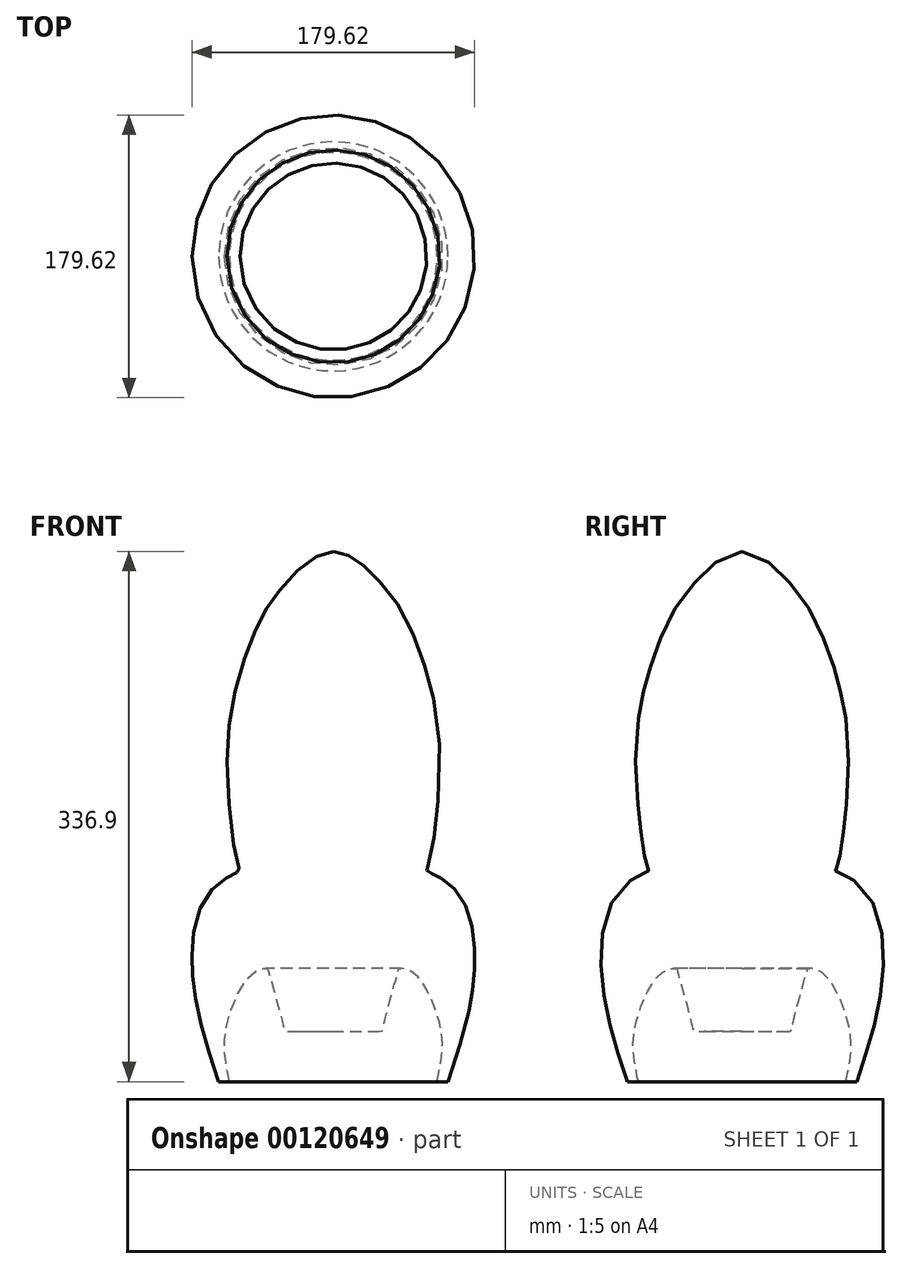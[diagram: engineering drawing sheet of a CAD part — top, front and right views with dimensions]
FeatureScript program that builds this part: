
annotation { "Feature Type Name" : "Feature", "Feature Type Description" : "" }
export const myFeature = defineFeature(function(context is Context, id is Id, definition is map)
    precondition{}
    {
        {
            var Q0;
            Q0=qCreatedBy(makeId("Front.planeOp"),FACE);
            var sketch = newSketch(context, id + "F0", { "sketchPlane" : qUnion([Q0])});
            skLineSegment(sketch, "E0", {"start": v(0, 114.68) * mm, "end": v(0, -121.07) * mm, "construction": true});
            skPoint(sketch, "E1", {"position": v(0, 172.24) * mm});
            skFitSpline(sketch, "E2", {"points": [v(-72.77, -166.31) * mm, v(-84.52, -128.06) * mm, v(-89.05, -101.48) * mm, v(-89.66, -81.76) * mm, v(-84.76, -56.41) * mm, v(-72.5, -39.7) * mm, v(-63.44, -34.55) * mm, v(-60.38, -33.08) * mm, v(-59.4, -32.71) * mm, v(-60.25, -30.02) * mm, v(-67.36, 26.2) * mm, v(-61.85, 84.61) * mm, v(-47.02, 126) * mm, v(-35.24, 144.53) * mm, v(-13.84, 165.57) * mm, v(0, 170.6) * mm], "startDerivative": vector(-145.39, 429.1) * mm, "endDerivative": vector(234.13, 44.8) * mm});
            skLineSegment(sketch, "E3", {"start": v(-72.77, -166.31) * mm, "end": v(-65.98, -166.31) * mm});
            skFitSpline(sketch, "E4", {"points": [v(-65.98, -166.31) * mm, v(-68.4, -152.9) * mm, v(-68.22, -132.99) * mm, v(-52.46, -98.52) * mm, v(-43.36, -94.29) * mm, v(-42.42, -94.32) * mm, v(-41.67, -94.42) * mm, v(-41.45, -95.04) * mm, v(-39.3, -102.66) * mm, v(-33.95, -122.35) * mm, v(-31.41, -132.76) * mm, v(-31.12, -133.88) * mm, v(-30.78, -134.17) * mm, v(-29.95, -134.31) * mm, v(0, -134.22) * mm], "startDerivative": vector(-30, 143.6) * mm, "endDerivative": vector(307.28, 2.8) * mm});
            skLineSegment(sketch, "E5", {"start": v(0, 170.6) * mm, "end": v(0, -134.22) * mm});
            skSolve(sketch);
        }
        {
            var Q0;
            Q0=makeQuery(id+"F0.imprint","IMPRINT",FACE,{"disambiguationData":[TD([[makeQuery(id+"F0.imprint","IMPRINT",EDGE,{"derivedFrom":sQuery(id+"F0.wireOp",EDGE,"E2")}),-1.0]])]});
            var Q1;
            Q1=sQuery(id+"F0.wireOp",EDGE,"E5");
            revolve(context, id + "F1", {"entities" : qUnion([Q0]), "axis" : qUnion([Q1]), "revolveType" : RevolveType.SYMMETRIC, "angle" : 360 * degree});
        }
    });
